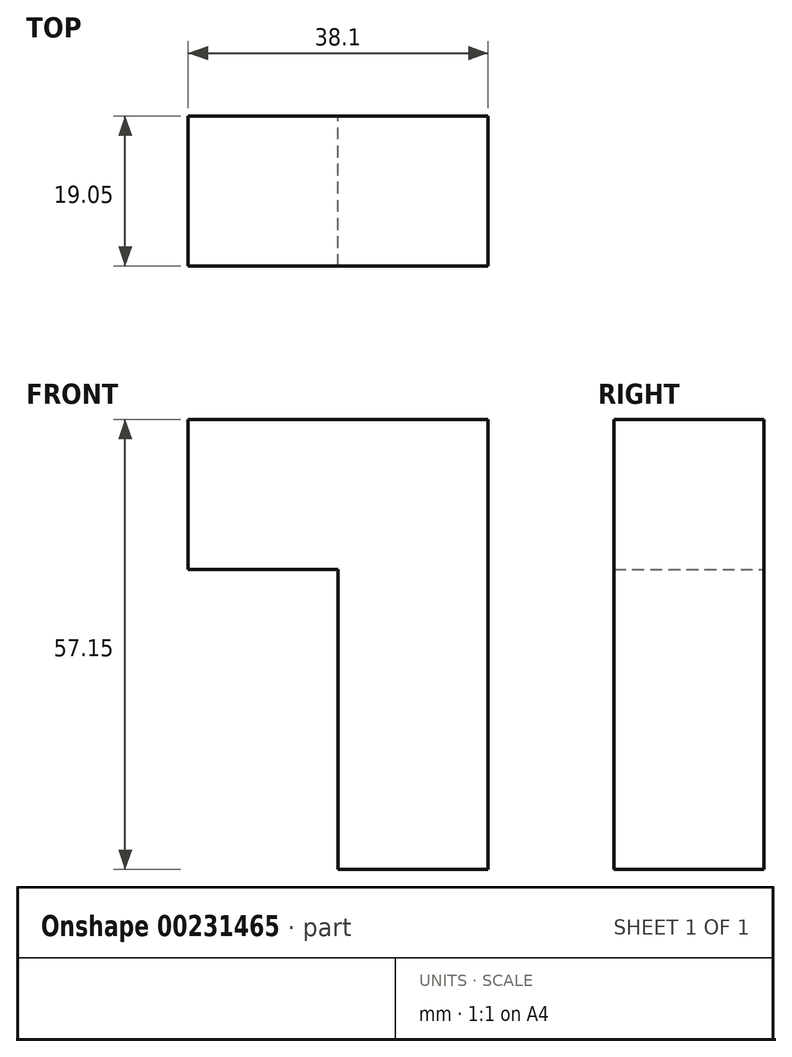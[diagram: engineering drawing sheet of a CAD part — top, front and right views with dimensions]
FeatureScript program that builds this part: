
annotation { "Feature Type Name" : "Feature", "Feature Type Description" : "" }
export const myFeature = defineFeature(function(context is Context, id is Id, definition is map)
    precondition{}
    {
        {
            var Q0;
            Q0=qCreatedBy(makeId("Front.planeOp"),FACE);
            var sketch = newSketch(context, id + "F0", { "sketchPlane" : qUnion([Q0])});
            skLineSegment(sketch, "E0.bottom", {"start": v(-71.48, 57.15) * mm, "end": v(-52.43, 57.15) * mm});
            skLineSegment(sketch, "E0.top", {"start": v(-71.48, 38.1) * mm, "end": v(-52.43, 38.1) * mm});
            skLineSegment(sketch, "E0.left", {"start": v(-71.48, 57.15) * mm, "end": v(-71.48, 38.1) * mm});
            skLineSegment(sketch, "E0.right", {"start": v(-52.43, 57.15) * mm, "end": v(-52.43, 38.1) * mm});
            skLineSegment(sketch, "E1.bottom", {"start": v(-52.43, 57.15) * mm, "end": v(-33.38, 57.15) * mm});
            skLineSegment(sketch, "E1.top", {"start": v(-52.43, 0) * mm, "end": v(-33.38, 0) * mm});
            skLineSegment(sketch, "E1.left", {"start": v(-52.43, 57.15) * mm, "end": v(-52.43, 0) * mm});
            skLineSegment(sketch, "E1.right", {"start": v(-33.38, 57.15) * mm, "end": v(-33.38, 0) * mm});
            skSolve(sketch);
        }
        {
            var Q0;
            {var subQ3=sQuery(id+"F0.wireOp",EDGE,"E1.bottom");Q0=makeQuery(id+"F0.imprint","IMPRINT",FACE,{"disambiguationData":[TD([[makeQuery(id+"F0.imprint","IMPRINT",EDGE,{"derivedFrom":subQ3}),-1.0]])]});}
            var Q1;
            {var subQ0=sQuery(id+"F0.wireOp",EDGE,"E0.bottom");Q1=makeQuery(id+"F0.imprint","IMPRINT",FACE,{"disambiguationData":[TD([[makeQuery(id+"F0.imprint","IMPRINT",EDGE,{"derivedFrom":subQ0}),-1.0]])]});}
            extrude(context, id + "F1", {"entities" : qUnion([Q0, Q1]), "depth" : 19.05 * mm});
        }
    });
